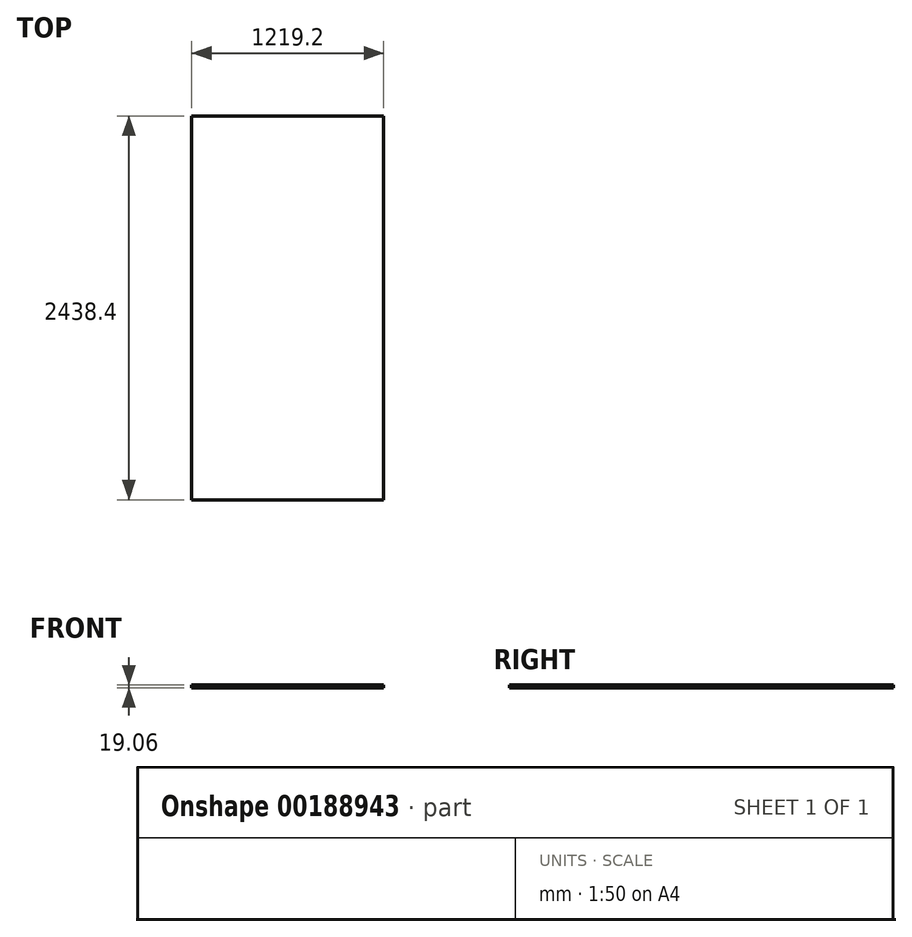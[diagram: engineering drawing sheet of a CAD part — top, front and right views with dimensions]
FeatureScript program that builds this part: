
annotation { "Feature Type Name" : "Feature", "Feature Type Description" : "" }
export const myFeature = defineFeature(function(context is Context, id is Id, definition is map)
    precondition{}
    {
        {
            var Q0;
            Q0=qCreatedBy(makeId("Top.planeOp"),FACE);
            var sketch = newSketch(context, id + "F1", { "sketchPlane" : qUnion([Q0])});
            skLineSegment(sketch, "E0.bottom", {"start": v(609.6, -1219.2) * mm, "end": v(-609.6, -1219.2) * mm});
            skLineSegment(sketch, "E0.top", {"start": v(609.6, 1219.2) * mm, "end": v(-609.6, 1219.2) * mm});
            skLineSegment(sketch, "E0.left", {"start": v(609.6, -1219.2) * mm, "end": v(609.6, 1219.2) * mm});
            skLineSegment(sketch, "E0.right", {"start": v(-609.6, -1219.2) * mm, "end": v(-609.6, 1219.2) * mm});
            skPoint(sketch, "E0.middle", {"position": v(0, 0) * mm});
            skSolve(sketch);
        }
        {
            var Q0;
            Q0=makeQuery(id+"F1.imprint","IMPRINT",FACE,{"disambiguationData":[TD([[makeQuery(id+"F1.imprint","IMPRINT",EDGE,{"derivedFrom":sQuery(id+"F1.wireOp",EDGE,"E0.bottom")}),-1.0]])]});
            extrude(context, id + "F0", {"entities" : qUnion([Q0]), "endBound" : BoundingType.SYMMETRIC, "depth" : 19.05 * mm});
        }
    });
